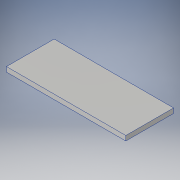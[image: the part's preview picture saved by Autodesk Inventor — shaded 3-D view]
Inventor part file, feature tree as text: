
AUTODESK INVENTOR PART (.ipt)
format: ipt  version: 2019 (Build 230136000, 136)  size: 91,136 bytes
history: native  units: in
note: dims shown in document units (in); Inventor stores cm internally (conversion verified against a paired STEP export)
features: other x1, extrude x1, sketch x1
ambient origin geometry x8: Origin, YZ Plane, XZ Plane, XY Plane, X Axis, Y Axis, Z Axis, Center Point
bodies: Solid1 (feature_tree)
feature tree (3):
  other  "bucket holder plate"
  extrude  "Extrusion1"  Depth=1.25in
  sketch  "Sketch1"  dims[d0=3.125in d1=1.25in d2=0.125in d3=0.0in]
